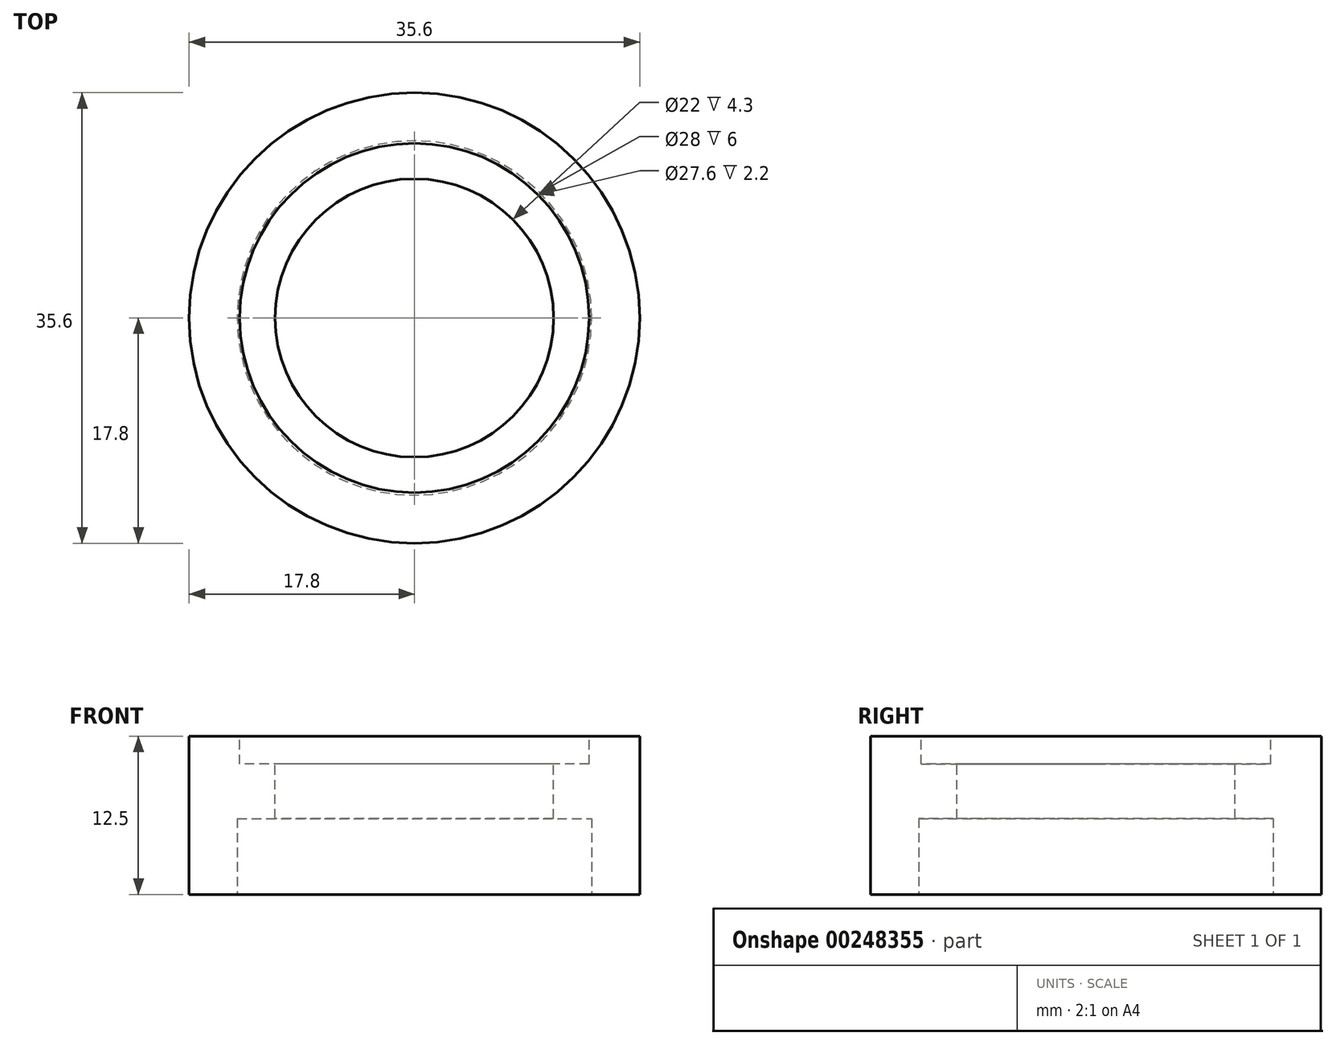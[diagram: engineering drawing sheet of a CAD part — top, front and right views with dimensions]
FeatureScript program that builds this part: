
annotation { "Feature Type Name" : "Feature", "Feature Type Description" : "" }
export const myFeature = defineFeature(function(context is Context, id is Id, definition is map)
    precondition{}
    {
        {
            var Q0;
            Q0=qCreatedBy(makeId("Top.planeOp"),FACE);
            var sketch = newSketch(context, id + "F0", { "sketchPlane" : qUnion([Q0])});
            skCircle(sketch, "E0", {"center": v(0, 0) * mm, "radius": 17.8 * mm});
            skSolve(sketch);
        }
        {
            var Q0;
            Q0 = qSketchRegion(id + "F0", true);
            extrude(context, id + "F1", {"entities" : qUnion([Q0]), "depth" : 12.5 * mm});
        }
        {
            var Q0;
            Q0=makeQuery(id+"F1.opExtrude","CAP_FACE",FACE,{"disambiguationData":[OSD([sQuery(id+"F0.wireOp",EDGE,"E0")])],"isStart":false});
            var sketch = newSketch(context, id + "F2", { "sketchPlane" : qUnion([Q0])});
            skCircle(sketch, "E1", {"center": v(0, 0) * mm, "radius": 11 * mm});
            skSolve(sketch);
        }
        {
            var Q0;
            Q0 = qSketchRegion(id + "F2", true);
            extrude(context, id + "F3", {"entities" : qUnion([Q0]), "operationType" : NewBodyOperationType.REMOVE, "oppositeDirection" : true, "depth" : 25 * mm});
        }
        {
            var Q0;
            Q0=makeQuery(id+"F1.opExtrude","CAP_FACE",FACE,{"disambiguationData":[OSD([sQuery(id+"F0.wireOp",EDGE,"E0")])],"isStart":true});
            var sketch = newSketch(context, id + "F4", { "sketchPlane" : qUnion([Q0])});
            skCircle(sketch, "E2", {"center": v(0, 0) * mm, "radius": 14 * mm});
            skSolve(sketch);
        }
        {
            var Q0;
            Q0 = qSketchRegion(id + "F4", true);
            extrude(context, id + "F5", {"entities" : qUnion([Q0]), "operationType" : NewBodyOperationType.REMOVE, "oppositeDirection" : true, "depth" : 6 * mm});
        }
        {
            var Q0;
            Q0=makeQuery(id+"F1.opExtrude","CAP_FACE",FACE,{"disambiguationData":[OSD([sQuery(id+"F0.wireOp",EDGE,"E0")])],"isStart":false});
            var sketch = newSketch(context, id + "F6", { "sketchPlane" : qUnion([Q0])});
            skCircle(sketch, "E3", {"center": v(0, 0) * mm, "radius": 13.8 * mm});
            skSolve(sketch);
        }
        {
            var Q0;
            Q0 = qSketchRegion(id + "F6", true);
            extrude(context, id + "F7", {"entities" : qUnion([Q0]), "operationType" : NewBodyOperationType.REMOVE, "oppositeDirection" : true, "depth" : 2.2 * mm});
        }
    });
